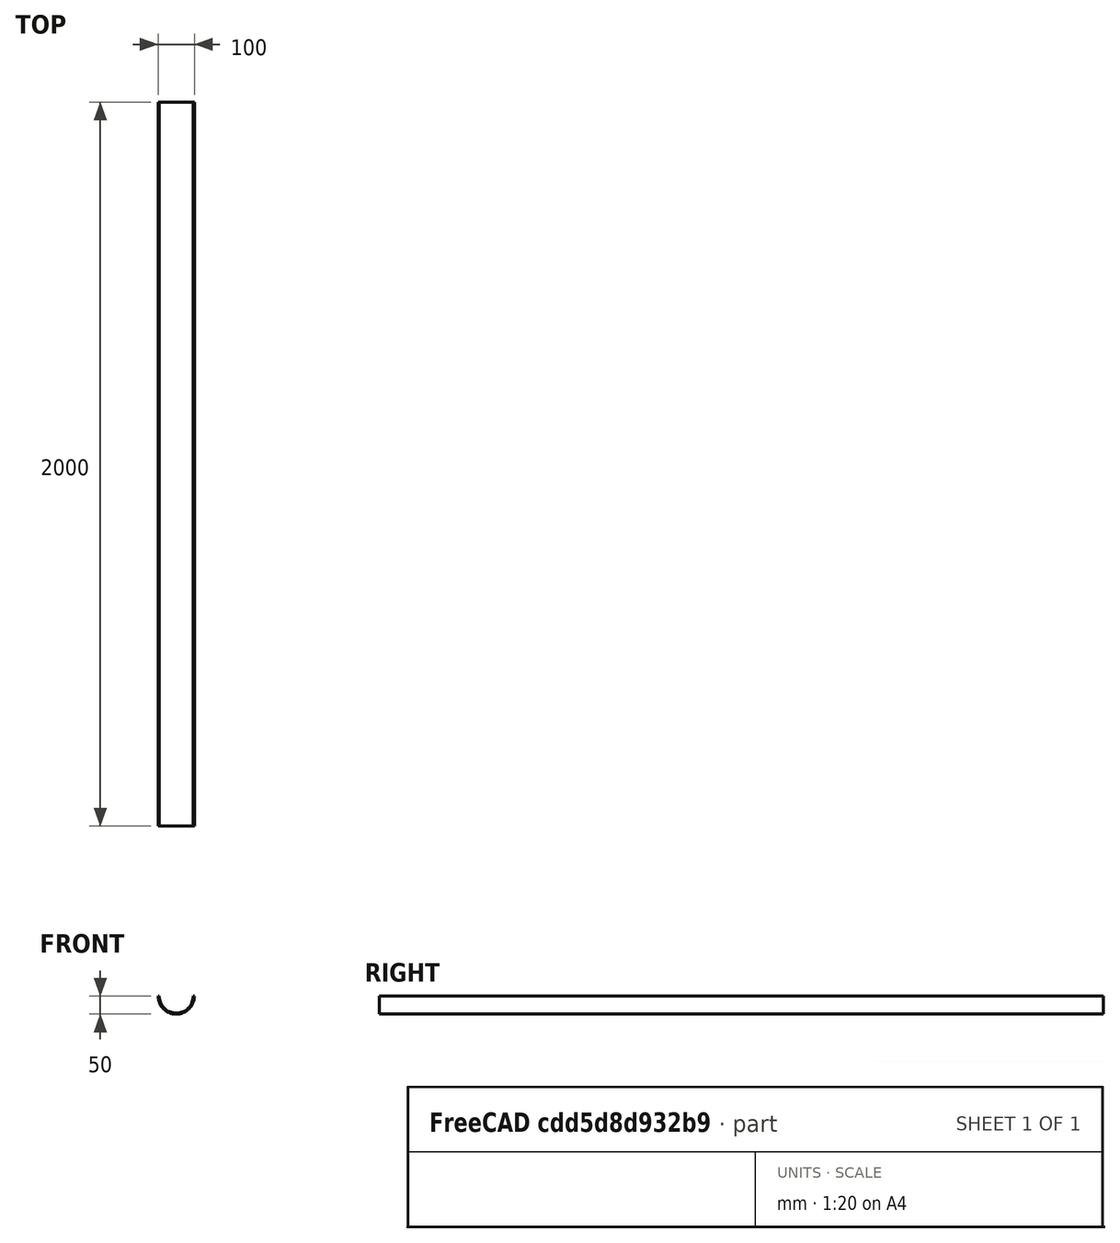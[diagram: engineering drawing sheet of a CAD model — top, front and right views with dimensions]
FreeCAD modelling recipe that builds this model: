
FCSTD DOCUMENT  (FreeCAD 0.15R4671 (Git))
Label: Demi_tube_sous_miroir_old
License: All rights reserved
LicenseURL: http://en.wikipedia.org/wiki/All_rights_reserved
objects: Sketcher::SketchObject×1, PartDesign::Pad×1
note: 3 computed .brp shape members not serialized (recipe doc carries the construction recipe); baked Part::Feature solids carry a one-line shape summary decoded from their .brp

FEATURE [Sketcher::SketchObject] Sketch
  Placement = pos=(0,0,0) rot=(1,0,0;1.5708rad)
  sketch-geometry (4):
    g0: LineSegment StartX=-50 StartY=0 StartZ=0 EndX=-47 EndY=0 EndZ=0
    g1: LineSegment StartX=47 StartY=0 StartZ=0 EndX=50 EndY=0 EndZ=0
    g2: ArcOfCircle CenterX=0 CenterY=0 CenterZ=0 NormalX=0 NormalY=0 NormalZ=1 Radius=47 StartAngle=3.14159 EndAngle=6.28319
    g3: ArcOfCircle CenterX=0 CenterY=0 CenterZ=0 NormalX=0 NormalY=0 NormalZ=1 Radius=50 StartAngle=3.14159 EndAngle=6.28319
  constraints (13):
    c: Horizontal(g0)
    c: PointOnObject(g1,g-1)
    c: Horizontal(g1)
    c: Coincident(g2,g-1)
    c: PointOnObject(g2,g-1)
    c: Coincident(g3,g-1)
    c: Coincident(g3,g1)
    c: PointOnObject(g3,g-1)
    c: Coincident(g0,g3)
    c: Coincident(g0,g2)
    c: Distance(g0,g1) = 100
    c: Distance(g0,g0) = 3
    c: Coincident(g1,g2)
FEATURE [PartDesign::Pad] Pad
  Length = 2000
  Length2 = 100
  Midplane = true
  Placement = pos=(0,0,0) rot=(1,0,0;1.5708rad)
  Sketch = -> Sketch
  Type = 0
